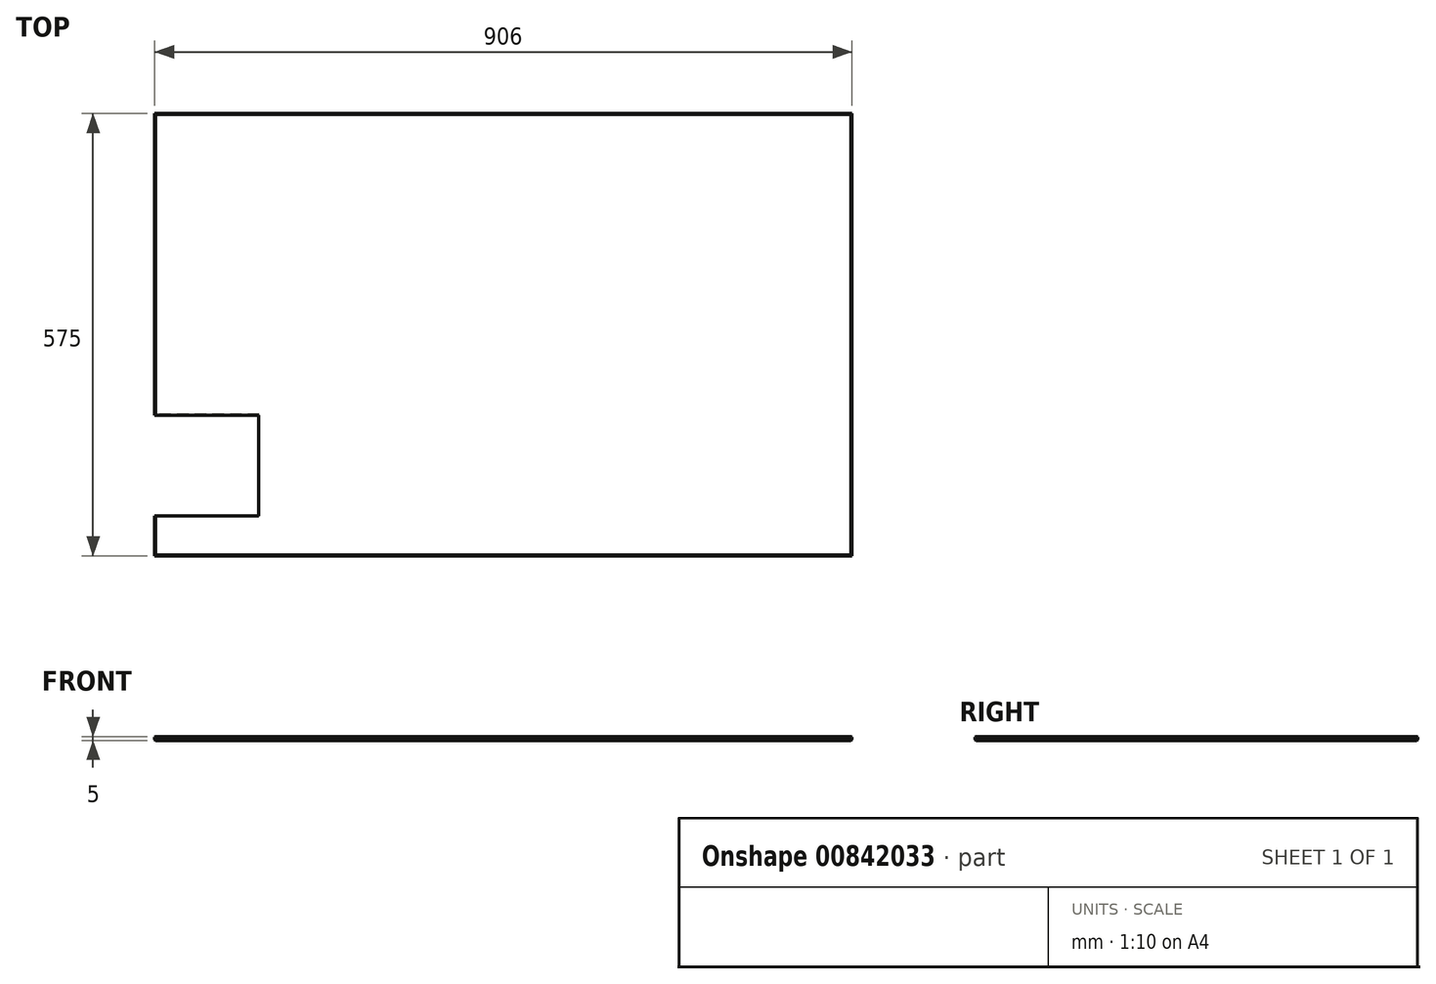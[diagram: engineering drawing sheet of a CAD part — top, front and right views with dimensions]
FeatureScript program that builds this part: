
annotation { "Feature Type Name" : "Feature", "Feature Type Description" : "" }
export const myFeature = defineFeature(function(context is Context, id is Id, definition is map)
    precondition{}
    {
        {
            var Q0;
            Q0=qCreatedBy(makeId("Top.planeOp"),FACE);
            var sketch = newSketch(context, id + "F0", { "sketchPlane" : qUnion([Q0])});
            skLineSegment(sketch, "E0.bottom", {"start": v(-453, 287.5) * mm, "end": v(453, 287.5) * mm});
            skLineSegment(sketch, "E0.top", {"start": v(-453, -287.5) * mm, "end": v(453, -287.5) * mm});
            skLineSegment(sketch, "E0.left", {"start": v(-453, 287.5) * mm, "end": v(-453, -287.5) * mm});
            skLineSegment(sketch, "E0.right", {"start": v(453, 287.5) * mm, "end": v(453, -287.5) * mm});
            skPoint(sketch, "E0.middle", {"position": v(0, 0) * mm});
            skSolve(sketch);
        }
        {
            var Q0;
            Q0=makeQuery(id+"F0.imprint","IMPRINT",FACE,{"disambiguationData":[TD([[makeQuery(id+"F0.imprint","IMPRINT",EDGE,{"derivedFrom":sQuery(id+"F0.wireOp",EDGE,"E0.bottom")}),-1.0]])]});
            extrude(context, id + "F1", {"entities" : qUnion([Q0]), "endBound" : BoundingType.SYMMETRIC, "depth" : 5 * mm, "offsetDistance" : 25 * mm});
        }
        {
            var Q0;
            Q0=makeQuery(id+"F1.opExtrude","CAP_FACE",FACE,{"disambiguationData":[OSD([sQuery(id+"F0.wireOp",EDGE,"E0.bottom"),sQuery(id+"F0.wireOp",EDGE,"E0.top"),sQuery(id+"F0.wireOp",EDGE,"E0.left"),sQuery(id+"F0.wireOp",EDGE,"E0.right")])],"isStart":false});
            var sketch = newSketch(context, id + "F2", { "sketchPlane" : qUnion([Q0])});
            skLineSegment(sketch, "E1.bottom", {"start": v(-454, -104.5) * mm, "end": v(-318, -104.5) * mm});
            skLineSegment(sketch, "E1.top", {"start": v(-454, -235.5) * mm, "end": v(-318, -235.5) * mm});
            skLineSegment(sketch, "E1.left", {"start": v(-454, -104.5) * mm, "end": v(-454, -235.5) * mm});
            skLineSegment(sketch, "E1.right", {"start": v(-318, -104.5) * mm, "end": v(-318, -235.5) * mm});
            skSolve(sketch);
        }
        {
            var Q0;
            Q0=makeQuery(id+"F2.imprint","IMPRINT",FACE,{"disambiguationData":[TD([[makeQuery(id+"F2.imprint","IMPRINT",EDGE,{"derivedFrom":sQuery(id+"F2.wireOp",EDGE,"E1.bottom")}),-1.0]])]});
            extrude(context, id + "F3", {"entities" : qUnion([Q0]), "operationType" : NewBodyOperationType.REMOVE, "endBound" : BoundingType.THROUGH_ALL, "oppositeDirection" : true, "depth" : 25 * mm, "offsetDistance" : 25 * mm});
        }
        {
            var Q0;
            {var subQ0=sQuery(id+"F0.wireOp",EDGE,"E0.bottom");var subQ1=sQuery(id+"F0.wireOp",EDGE,"E0.left");Q0=makeQuery(id+"F3.boolean.opBoolean","SPLIT",EDGE,{"disambiguationData":[TD([makeQuery(id+"F1.opExtrude","SWEPT_FACE",FACE,{"disambiguationData":[OSD([subQ0])]})])],"derivedFrom":makeQuery(id+"F1.opExtrude","CAP_EDGE",EDGE,{"disambiguationData":[OSD([subQ1])],"isStart":false})});}
            var Q1;
            {var subQ0=sQuery(id+"F0.wireOp",EDGE,"E0.bottom");var subQ1=sQuery(id+"F0.wireOp",EDGE,"E0.left");Q1=makeQuery(id+"F3.boolean.opBoolean","SPLIT",EDGE,{"disambiguationData":[TD([makeQuery(id+"F1.opExtrude","SWEPT_FACE",FACE,{"disambiguationData":[OSD([subQ0])]})])],"derivedFrom":makeQuery(id+"F1.opExtrude","CAP_EDGE",EDGE,{"disambiguationData":[OSD([subQ1])],"isStart":true})});}
            var Q2;
            {var subQ0=sQuery(id+"F0.wireOp",EDGE,"E0.left");var subQ1=sQuery(id+"F0.wireOp",EDGE,"E0.top");Q2=makeQuery(id+"F3.boolean.opBoolean","SPLIT",EDGE,{"disambiguationData":[TD([makeQuery(id+"F1.opExtrude","SWEPT_FACE",FACE,{"disambiguationData":[OSD([subQ1])]})])],"derivedFrom":makeQuery(id+"F1.opExtrude","CAP_EDGE",EDGE,{"disambiguationData":[OSD([subQ0])],"isStart":true})});}
            var Q3;
            {var subQ0=sQuery(id+"F0.wireOp",EDGE,"E0.left");var subQ1=sQuery(id+"F0.wireOp",EDGE,"E0.top");Q3=makeQuery(id+"F3.boolean.opBoolean","SPLIT",EDGE,{"disambiguationData":[TD([makeQuery(id+"F1.opExtrude","SWEPT_FACE",FACE,{"disambiguationData":[OSD([subQ1])]})])],"derivedFrom":makeQuery(id+"F1.opExtrude","CAP_EDGE",EDGE,{"disambiguationData":[OSD([subQ0])],"isStart":false})});}
            var Q4;
            Q4=makeQuery(id+"F1.opExtrude","CAP_EDGE",EDGE,{"disambiguationData":[OSD([sQuery(id+"F0.wireOp",EDGE,"E0.top")])],"isStart":true});
            var Q5;
            Q5=makeQuery(id+"F1.opExtrude","CAP_EDGE",EDGE,{"disambiguationData":[OSD([sQuery(id+"F0.wireOp",EDGE,"E0.top")])],"isStart":false});
            var Q6;
            Q6=makeQuery(id+"F1.opExtrude","CAP_EDGE",EDGE,{"disambiguationData":[OSD([sQuery(id+"F0.wireOp",EDGE,"E0.right")])],"isStart":false});
            var Q7;
            Q7=makeQuery(id+"F1.opExtrude","CAP_EDGE",EDGE,{"disambiguationData":[OSD([sQuery(id+"F0.wireOp",EDGE,"E0.right")])],"isStart":true});
            var Q8;
            Q8=makeQuery(id+"F1.opExtrude","CAP_EDGE",EDGE,{"disambiguationData":[OSD([sQuery(id+"F0.wireOp",EDGE,"E0.bottom")])],"isStart":false});
            var Q9;
            Q9=makeQuery(id+"F1.opExtrude","CAP_EDGE",EDGE,{"disambiguationData":[OSD([sQuery(id+"F0.wireOp",EDGE,"E0.bottom")])],"isStart":true});
            var Q10;
            Q10=makeQuery(id+"F3.boolean.opBoolean","COPY",EDGE,{"derivedFrom":makeQuery(id+"F3.opExtrude","CAP_EDGE",EDGE,{"disambiguationData":[OSD([sQuery(id+"F2.wireOp",EDGE,"E1.bottom")])],"isStart":true})});
            var Q11;
            Q11=makeQuery(id+"F3.boolean.opBoolean","INTERSECT",EDGE,{"derivedFrom":[makeQuery(id+"F1.opExtrude","CAP_FACE",FACE,{"disambiguationData":[OSD([sQuery(id+"F0.wireOp",EDGE,"E0.bottom"),sQuery(id+"F0.wireOp",EDGE,"E0.top"),sQuery(id+"F0.wireOp",EDGE,"E0.left"),sQuery(id+"F0.wireOp",EDGE,"E0.right")])],"isStart":true}),makeQuery(id+"F3.opExtrude","SWEPT_FACE",FACE,{"disambiguationData":[OSD([sQuery(id+"F2.wireOp",EDGE,"E1.bottom")])]})]});
            var Q12;
            Q12=makeQuery(id+"F3.boolean.opBoolean","INTERSECT",EDGE,{"derivedFrom":[makeQuery(id+"F1.opExtrude","CAP_FACE",FACE,{"disambiguationData":[OSD([sQuery(id+"F0.wireOp",EDGE,"E0.bottom"),sQuery(id+"F0.wireOp",EDGE,"E0.top"),sQuery(id+"F0.wireOp",EDGE,"E0.left"),sQuery(id+"F0.wireOp",EDGE,"E0.right")])],"isStart":true}),makeQuery(id+"F3.opExtrude","SWEPT_FACE",FACE,{"disambiguationData":[OSD([sQuery(id+"F2.wireOp",EDGE,"E1.right")])]})]});
            var Q13;
            Q13=makeQuery(id+"F3.boolean.opBoolean","COPY",EDGE,{"derivedFrom":makeQuery(id+"F3.opExtrude","CAP_EDGE",EDGE,{"disambiguationData":[OSD([sQuery(id+"F2.wireOp",EDGE,"E1.right")])],"isStart":true})});
            var Q14;
            Q14=makeQuery(id+"F3.boolean.opBoolean","COPY",EDGE,{"derivedFrom":makeQuery(id+"F3.opExtrude","CAP_EDGE",EDGE,{"disambiguationData":[OSD([sQuery(id+"F2.wireOp",EDGE,"E1.top")])],"isStart":true})});
            var Q15;
            Q15=makeQuery(id+"F3.boolean.opBoolean","INTERSECT",EDGE,{"derivedFrom":[makeQuery(id+"F1.opExtrude","CAP_FACE",FACE,{"disambiguationData":[OSD([sQuery(id+"F0.wireOp",EDGE,"E0.bottom"),sQuery(id+"F0.wireOp",EDGE,"E0.top"),sQuery(id+"F0.wireOp",EDGE,"E0.left"),sQuery(id+"F0.wireOp",EDGE,"E0.right")])],"isStart":true}),makeQuery(id+"F3.opExtrude","SWEPT_FACE",FACE,{"disambiguationData":[OSD([sQuery(id+"F2.wireOp",EDGE,"E1.top")])]})]});
            chamfer(context, id + "F4", {"entities" : qUnion([Q0, Q1, Q2, Q3, Q4, Q5, Q6, Q7, Q8, Q9, Q10, Q11, Q12, Q13, Q14, Q15]), "width" : 1 * mm, "tangentPropagation" : true});
        }
    });
